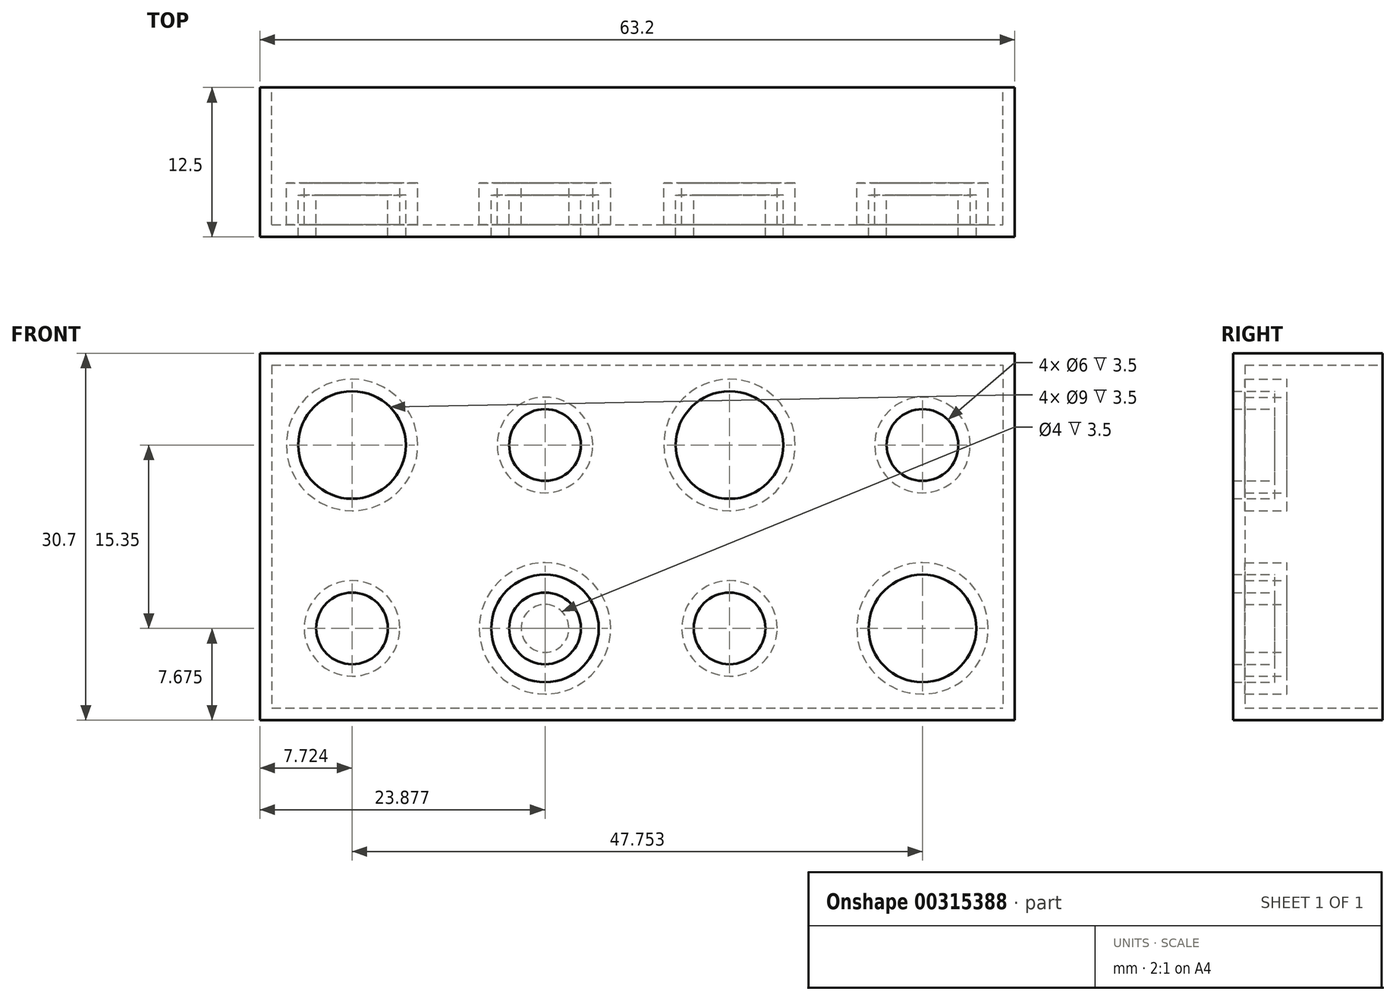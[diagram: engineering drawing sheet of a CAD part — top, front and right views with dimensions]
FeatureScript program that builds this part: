
annotation { "Feature Type Name" : "Feature", "Feature Type Description" : "" }
export const myFeature = defineFeature(function(context is Context, id is Id, definition is map)
    precondition{}
    {
        {
            var Q0;
            Q0=qCreatedBy(makeId("Front.planeOp"),FACE);
            var sketch = newSketch(context, id + "F0", { "sketchPlane" : qUnion([Q0])});
            skLineSegment(sketch, "E0.bottom", {"start": v(-28.8, 15.35) * mm, "end": v(34.4, 15.35) * mm});
            skLineSegment(sketch, "E0.top", {"start": v(-28.8, -15.35) * mm, "end": v(34.4, -15.35) * mm});
            skLineSegment(sketch, "E0.left", {"start": v(-28.8, 15.35) * mm, "end": v(-28.8, -15.35) * mm});
            skLineSegment(sketch, "E0.right", {"start": v(34.4, 15.35) * mm, "end": v(34.4, -15.35) * mm});
            skPoint(sketch, "E0.middle", {"position": v(2.8, 0) * mm});
            skSolve(sketch);
        }
        {
            var Q0;
            Q0=makeQuery(id+"F0.imprint","IMPRINT",FACE,{"disambiguationData":[TD([[makeQuery(id+"F0.imprint","IMPRINT",EDGE,{"derivedFrom":sQuery(id+"F0.wireOp",EDGE,"E0.bottom")}),-1.0]])]});
            extrude(context, id + "F1", {"entities" : qUnion([Q0]), "depth" : 9 * mm});
        }
        {
            var Q0;
            Q0=makeQuery(id+"F1.opExtrude","CAP_FACE",FACE,{"disambiguationData":[OSD([sQuery(id+"F0.wireOp",EDGE,"E0.bottom"),sQuery(id+"F0.wireOp",EDGE,"E0.top"),sQuery(id+"F0.wireOp",EDGE,"E0.left"),sQuery(id+"F0.wireOp",EDGE,"E0.right")])],"isStart":false});
            var sketch = newSketch(context, id + "F2", { "sketchPlane" : qUnion([Q0])});
            skLineSegment(sketch, "E1.0.0", {"start": v(-28.8, 15.35) * mm, "end": v(-28.8, 0) * mm});
            skLineSegment(sketch, "E1.0.1", {"start": v(-28.8, -15.35) * mm, "end": v(34.4, -15.35) * mm});
            skLineSegment(sketch, "E1.0.2", {"start": v(34.4, -15.35) * mm, "end": v(34.4, 15.35) * mm});
            skLineSegment(sketch, "E1.0.3", {"start": v(34.4, 15.35) * mm, "end": v(-28.8, 15.35) * mm});
            skLineSegment(sketch, "E2", {"start": v(-28.8, 0) * mm, "end": v(34.4, 0) * mm, "construction": true});
            skLineSegment(sketch, "E3", {"start": v(2.8, 15.35) * mm, "end": v(2.8, -15.35) * mm, "construction": true});
            skCircle(sketch, "E4", {"center": v(-4.93, 7.68) * mm, "radius": 4.5 * mm});
            skLineSegment(sketch, "E5", {"start": v(-28.8, 0) * mm, "end": v(-28.8, -15.35) * mm});
            skLineSegment(sketch, "E6", {"start": v(-28.8, 7.68) * mm, "end": v(2.8, 7.67) * mm, "construction": true});
            skCircle(sketch, "E7", {"center": v(-4.93, 7.68) * mm, "radius": 3 * mm});
            skLineSegment(sketch, "E8", {"start": v(-13, 7.68) * mm, "end": v(-13, 0) * mm, "construction": true});
            skCircle(sketch, "E9.MirrorC", {"center": v(-21.09, 7.68) * mm, "radius": 4.5 * mm});
            skCircle(sketch, "E10.MirrorC", {"center": v(-21.09, 7.68) * mm, "radius": 3 * mm});
            skCircle(sketch, "E11.MirrorC", {"center": v(-21.09, -7.67) * mm, "radius": 4.5 * mm});
            skCircle(sketch, "E12.MirrorC", {"center": v(-21.09, -7.67) * mm, "radius": 3 * mm});
            skCircle(sketch, "E13.MirrorC", {"center": v(-4.93, -7.67) * mm, "radius": 3 * mm});
            skCircle(sketch, "E14.MirrorC", {"center": v(-4.93, -7.67) * mm, "radius": 4.5 * mm});
            skCircle(sketch, "E15.MirrorC", {"center": v(10.51, 7.68) * mm, "radius": 4.5 * mm});
            skCircle(sketch, "E16.MirrorC", {"center": v(10.51, 7.68) * mm, "radius": 3 * mm});
            skCircle(sketch, "E17.MirrorC", {"center": v(26.67, 7.68) * mm, "radius": 4.5 * mm});
            skCircle(sketch, "E18.MirrorC", {"center": v(26.67, 7.68) * mm, "radius": 3 * mm});
            skCircle(sketch, "E19.MirrorC", {"center": v(26.67, -7.68) * mm, "radius": 4.5 * mm});
            skCircle(sketch, "E20.MirrorC", {"center": v(26.67, -7.68) * mm, "radius": 3 * mm});
            skCircle(sketch, "E21.MirrorC", {"center": v(10.51, -7.67) * mm, "radius": 4.5 * mm});
            skCircle(sketch, "E22.MirrorC", {"center": v(10.51, -7.67) * mm, "radius": 3 * mm});
            skSolve(sketch);
        }
        {
            var Q0;
            Q0=makeQuery(id+"F2.imprint","IMPRINT",FACE,{"disambiguationData":[TD([[makeQuery(id+"F2.imprint","IMPRINT",EDGE,{"derivedFrom":sQuery(id+"F2.wireOp",EDGE,"E9.MirrorC")}),-1.0]])]});
            var Q1;
            Q1=makeQuery(id+"F2.imprint","IMPRINT",FACE,{"disambiguationData":[TD([[makeQuery(id+"F2.imprint","IMPRINT",EDGE,{"derivedFrom":sQuery(id+"F2.wireOp",EDGE,"E4")}),1.0]])]});
            var Q2;
            Q2=makeQuery(id+"F2.imprint","IMPRINT",FACE,{"disambiguationData":[TD([[makeQuery(id+"F2.imprint","IMPRINT",EDGE,{"derivedFrom":sQuery(id+"F2.wireOp",EDGE,"E15.MirrorC")}),-1.0]])]});
            var Q3;
            Q3=makeQuery(id+"F2.imprint","IMPRINT",FACE,{"disambiguationData":[TD([[makeQuery(id+"F2.imprint","IMPRINT",EDGE,{"derivedFrom":sQuery(id+"F2.wireOp",EDGE,"E13.MirrorC")}),1.0]])]});
            var Q4;
            Q4=makeQuery(id+"F2.imprint","IMPRINT",FACE,{"disambiguationData":[TD([[makeQuery(id+"F2.imprint","IMPRINT",EDGE,{"derivedFrom":sQuery(id+"F2.wireOp",EDGE,"E21.MirrorC")}),1.0]])]});
            var Q5;
            Q5=makeQuery(id+"F2.imprint","IMPRINT",FACE,{"disambiguationData":[TD([[makeQuery(id+"F2.imprint","IMPRINT",EDGE,{"derivedFrom":sQuery(id+"F2.wireOp",EDGE,"E11.MirrorC")}),1.0]])]});
            var Q6;
            Q6=makeQuery(id+"F2.imprint","IMPRINT",FACE,{"disambiguationData":[TD([[makeQuery(id+"F2.imprint","IMPRINT",EDGE,{"derivedFrom":sQuery(id+"F2.wireOp",EDGE,"E19.MirrorC")}),-1.0]])]});
            var Q7;
            Q7=makeQuery(id+"F2.imprint","IMPRINT",FACE,{"disambiguationData":[TD([[makeQuery(id+"F2.imprint","IMPRINT",EDGE,{"derivedFrom":sQuery(id+"F2.wireOp",EDGE,"E17.MirrorC")}),1.0]])]});
            extrude(context, id + "F3", {"entities" : qUnion([Q0, Q1, Q2, Q3, Q4, Q5, Q6, Q7]), "operationType" : NewBodyOperationType.ADD, "depth" : 3.5 * mm});
        }
        {
            var Q0;
            Q0=makeQuery(id+"F1.opExtrude","CAP_FACE",FACE,{"disambiguationData":[OSD([sQuery(id+"F0.wireOp",EDGE,"E0.bottom"),sQuery(id+"F0.wireOp",EDGE,"E0.top"),sQuery(id+"F0.wireOp",EDGE,"E0.left"),sQuery(id+"F0.wireOp",EDGE,"E0.right")])],"isStart":true});
            shell(context, id + "F4", {"entities" : qUnion([Q0]), "thickness" : 1 * mm});
        }
    });
